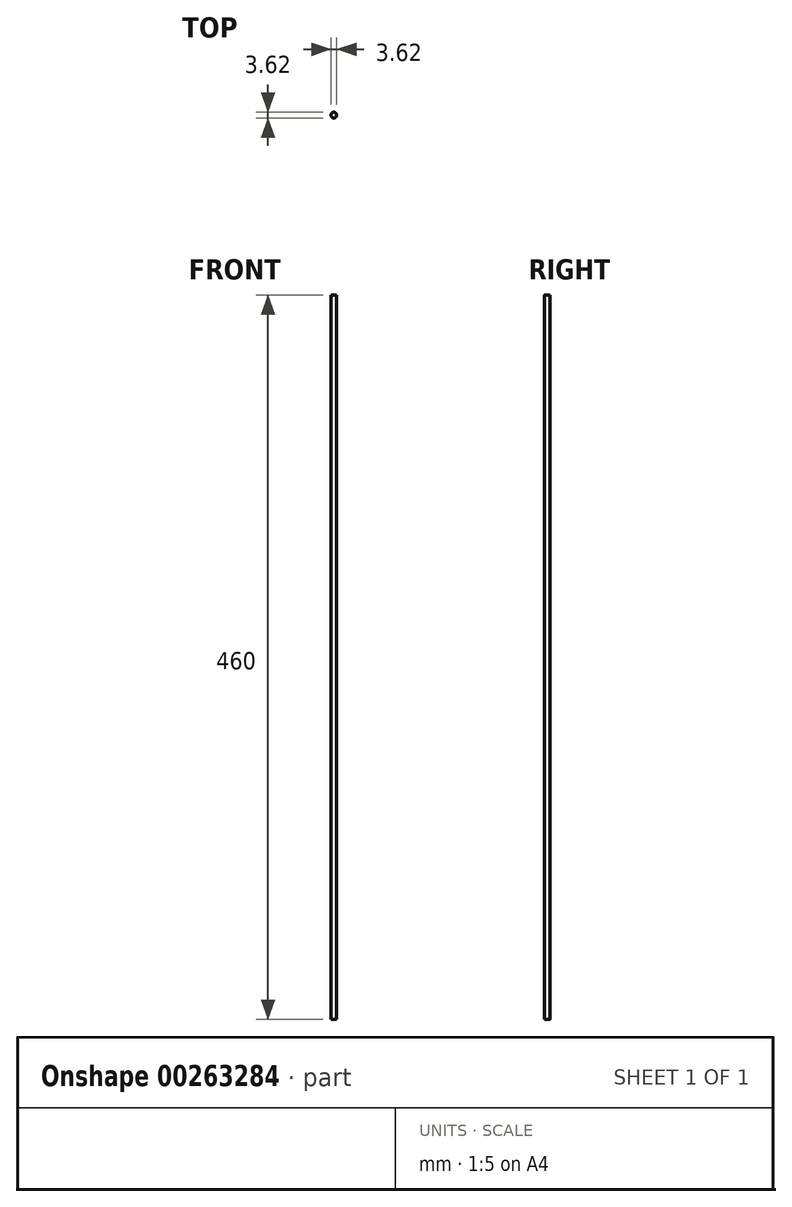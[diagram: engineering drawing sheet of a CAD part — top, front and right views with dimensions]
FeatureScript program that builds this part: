
annotation { "Feature Type Name" : "Feature", "Feature Type Description" : "" }
export const myFeature = defineFeature(function(context is Context, id is Id, definition is map)
    precondition{}
    {
        {
            var Q0;
            Q0=qCreatedBy(makeId("Top.planeOp"),FACE);
            var sketch = newSketch(context, id + "F0", { "sketchPlane" : qUnion([Q0])});
            skCircle(sketch, "E0", {"center": v(0, 0) * mm, "radius": 1.81 * mm});
            skSolve(sketch);
        }
        {
            var Q0;
            Q0 = qSketchRegion(id + "F0", true);
            extrude(context, id + "F1", {"entities" : qUnion([Q0]), "depth" : 460 * mm});
        }
    });
